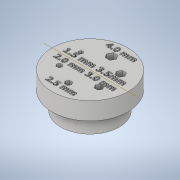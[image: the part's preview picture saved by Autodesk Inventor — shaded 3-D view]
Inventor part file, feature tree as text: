
AUTODESK INVENTOR PART (.ipt)
format: ipt  version: 2021 (Build 250183000, 183)  size: 921,088 bytes
history: native  units: in
note: dims shown in document units (in); Inventor stores cm internally (conversion verified against a paired STEP export)
features: extrude x4, sketch x4
ambient origin geometry x8: Origin, YZ Plane, XZ Plane, XY Plane, X Axis, Y Axis, Z Axis, Center Point
bodies: Solid1 (feature_tree)
feature tree (8):
  extrude  "Extrusion1"  Depth=0.375in TaperAngle=0.0deg
  extrude  "Extrusion2"  Depth=0.375in TaperAngle=0.0deg
  extrude  "Extrusion4"  Depth=2.3622in TaperAngle=360.0deg
  extrude  "Extrusion5"  Depth=0.1575in
  sketch  "Sketch1"  dims[d0=1.62in d1=0.375in d2=0.0in]
  sketch  "Sketch2"  dims[d3=1.25in d4=0.375in d5=0.0in]
  sketch  "Sketch5"  dims[d18=0.95in d19=2.3622in d21=360.0deg]
  sketch  "Sketch6"  dims[d23=0.1772in d24=0.1575in d25=0.1378in d26=0.1181in d27=0.0984in d28=0.0787in d29=0.0in d30=0.0in d31=0.6in d32=0.05in d33=0.155in d34=0.1875in d35=0.0in]
